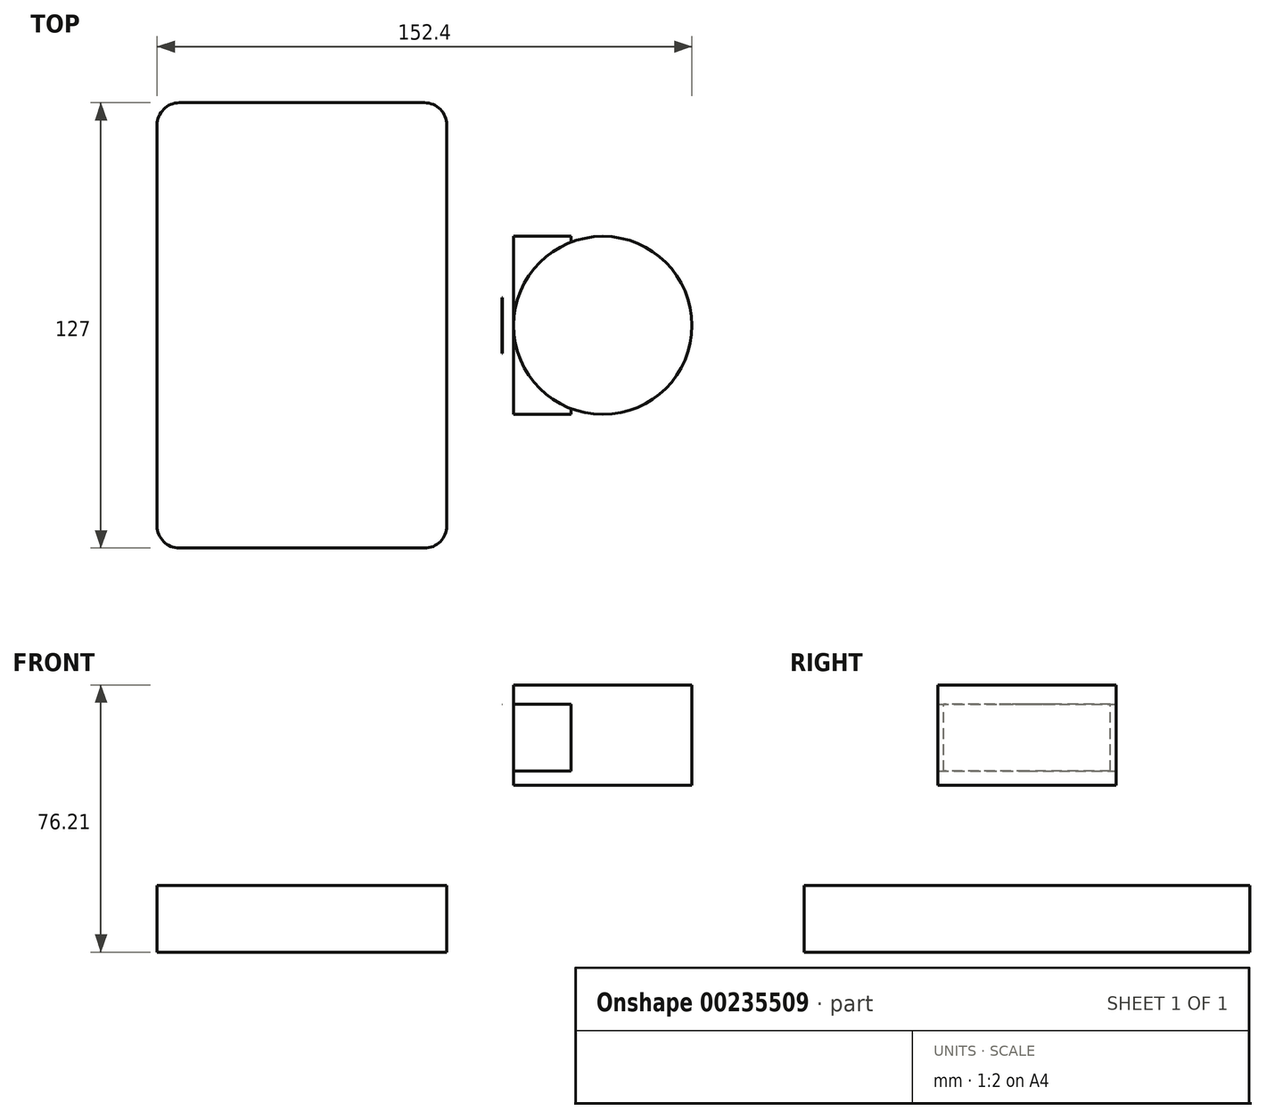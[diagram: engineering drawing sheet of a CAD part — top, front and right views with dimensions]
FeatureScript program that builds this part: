
annotation { "Feature Type Name" : "Feature", "Feature Type Description" : "" }
export const myFeature = defineFeature(function(context is Context, id is Id, definition is map)
    precondition{}
    {
        {
            var Q0;
            Q0=qCreatedBy(makeId("Front.planeOp"),FACE);
            var sketch = newSketch(context, id + "F0", { "sketchPlane" : qUnion([Q0])});
            skLineSegment(sketch, "E0.bottom", {"start": v(-41.28, 9.53) * mm, "end": v(41.28, 9.53) * mm});
            skLineSegment(sketch, "E0.top", {"start": v(-41.28, -9.53) * mm, "end": v(41.28, -9.53) * mm});
            skLineSegment(sketch, "E0.left", {"start": v(-41.28, 9.53) * mm, "end": v(-41.28, -9.53) * mm});
            skLineSegment(sketch, "E0.right", {"start": v(41.28, 9.53) * mm, "end": v(41.28, -9.53) * mm});
            skPoint(sketch, "E0.middle", {"position": v(0, 0) * mm});
            skLineSegment(sketch, "E1.bottom", {"start": v(60.32, 66.68) * mm, "end": v(111.12, 66.68) * mm});
            skLineSegment(sketch, "E1.top", {"start": v(60.33, 38.1) * mm, "end": v(111.12, 38.1) * mm});
            skLineSegment(sketch, "E1.left", {"start": v(60.32, 66.68) * mm, "end": v(60.33, 38.1) * mm});
            skLineSegment(sketch, "E1.right", {"start": v(111.12, 66.68) * mm, "end": v(111.12, 38.1) * mm});
            skPoint(sketch, "E1.middle", {"position": v(85.72, 52.39) * mm});
            skLineSegment(sketch, "E2", {"start": v(41.28, 9.53) * mm, "end": v(41.28, 26.23) * mm});
            skArc(sketch, "E3", {"start": v(41.28, 26.23) * mm, "mid": v(45.92, 37.46) * mm, "end": v(57.15, 42.1) * mm});
            skLineSegment(sketch, "E4", {"start": v(57.15, 42.1) * mm, "end": v(76.68, 42.1) * mm});
            skLineSegment(sketch, "E5.0", {"start": v(57.15, 61.16) * mm, "end": v(76.68, 61.16) * mm});
            skArc(sketch, "E5.1", {"start": v(22.23, 26.23) * mm, "mid": v(32.45, 50.93) * mm, "end": v(57.15, 61.16) * mm});
            skLineSegment(sketch, "E5.2", {"start": v(22.23, 9.53) * mm, "end": v(22.23, 26.23) * mm});
            skLineSegment(sketch, "E6", {"start": v(34.82, 16.42) * mm, "end": v(41.28, 17.88) * mm});
            skLineSegment(sketch, "E7", {"start": v(76.68, 66.68) * mm, "end": v(76.68, 38.1) * mm});
            skFitSpline(sketch, "E8", {"points": [v(-41.28, 9.53) * mm, v(57.15, 61.16) * mm], "startDerivative": vector(-0.8, 95.1) * mm, "endDerivative": vector(148.24, 0.28) * mm});
            skLineSegment(sketch, "E9", {"start": v(85.72, 66.68) * mm, "end": v(85.72, 38.1) * mm});
            skSolve(sketch);
        }
        {
            var Q0;
            Q0=makeQuery(id+"F0.imprint","IMPRINT",FACE,{"disambiguationData":[TD([[makeQuery(id+"F0.imprint","IMPRINT",EDGE,{"derivedFrom":sQuery(id+"F0.wireOp",EDGE,"E0.top")}),1.0]])]});
            extrude(context, id + "F1", {"entities" : qUnion([Q0]), "endBound" : BoundingType.SYMMETRIC, "depth" : 127 * mm});
        }
        {
            var Q0;
            {var subQ0=sQuery(id+"F0.wireOp",EDGE,"E5.0");var subQ1=sQuery(id+"F0.wireOp",EDGE,"E1.left");var subQ2=makeQuery(id+"F0.imprint","INTERSECT",VERTEX,{"derivedFrom":[subQ1,subQ0]});Q0=makeQuery(id+"F0.imprint","IMPRINT",FACE,{"disambiguationData":[TD([[makeQuery(id+"F0.imprint","IMPRINT",EDGE,{"disambiguationData":[TD([[subQ2,-1.0]])],"derivedFrom":subQ1}),1.0]])]});}
            var Q1;
            {var subQ0=sQuery(id+"F0.wireOp",EDGE,"E3");Q1=makeQuery(id+"F0.imprint","IMPRINT",FACE,{"disambiguationData":[TD([[makeQuery(id+"F0.imprint","IMPRINT",EDGE,{"derivedFrom":subQ0}),1.0]])]});}
            extrude(context, id + "F2", {"entities" : qUnion([Q0, Q1]), "operationType" : NewBodyOperationType.ADD, "endBound" : BoundingType.SYMMETRIC, "depth" : 50.8 * mm});
        }
        {
            var Q0;
            Q0=makeQuery(id+"F0.imprint","IMPRINT",FACE,{"disambiguationData":[TD([[makeQuery(id+"F0.imprint","IMPRINT",EDGE,{"derivedFrom":sQuery(id+"F0.wireOp",EDGE,"E5.1")}),1.0]])]});
            extrude(context, id + "F3", {"entities" : qUnion([Q0]), "operationType" : NewBodyOperationType.ADD, "endBound" : BoundingType.SYMMETRIC, "depth" : 15.88 * mm});
        }
        {
            var Q0;
            {var subQ0=sQuery(id+"F0.wireOp",EDGE,"E1.right");Q0=makeQuery(id+"F0.imprint","IMPRINT",FACE,{"disambiguationData":[TD([[makeQuery(id+"F0.imprint","IMPRINT",EDGE,{"derivedFrom":subQ0}),-1.0]])]});}
            var Q1;
            Q1=sQuery(id+"F0.wireOp",EDGE,"E9");
            revolve(context, id + "F4", {"entities" : qUnion([Q0]), "axis" : qUnion([Q1]), "revolveType" : RevolveType.FULL});
        }
        {
            var Q0;
            Q0=makeQuery(id+"F1.opExtrude","CAP_EDGE",EDGE,{"disambiguationData":[OSD([sQuery(id+"F0.wireOp",EDGE,"E0.left")])],"isStart":false});
            var Q1;
            Q1=makeQuery(id+"F1.opExtrude","CAP_EDGE",EDGE,{"disambiguationData":[OSD([sQuery(id+"F0.wireOp",EDGE,"E0.right")])],"isStart":false});
            var Q2;
            Q2=makeQuery(id+"F1.opExtrude","CAP_EDGE",EDGE,{"disambiguationData":[OSD([sQuery(id+"F0.wireOp",EDGE,"E0.right")])],"isStart":true});
            var Q3;
            Q3=makeQuery(id+"F1.opExtrude","CAP_EDGE",EDGE,{"disambiguationData":[OSD([sQuery(id+"F0.wireOp",EDGE,"E0.left")])],"isStart":true});
            fillet(context, id + "F5", {"entities" : qUnion([Q0, Q1, Q2, Q3]), "radius" : 6.35 * mm, "tangentPropagation" : true, "allowEdgeOverflow" : false});
        }
    });
